# Revit family: P190780JX-228c_JFC2089BEP_StainlessSteel_JA_Refrigeraton_FS_FDBM
name_source: partatom
category: Specialty Equipment
units: mm (PartAtom-declared; Revit-internal decimal feet)

## family parameters
Always vertical = Yes
Cut with Voids When Loaded = No
Enable Cutting in Views = No
Maintain Annotation Orientation = No
Part Type = Normal
Room Calculation Point = No
Round Connector Dimension = Use Diameter
Shared = No
Work Plane-Based = No

## types (1)
- JFC2089BEP
    Accent Material = ARCAT - Metal - Steel - Black
    Amps = 20 A
    Body Material = ARCAT - Metal - Steel - Stainless
    Clearance Material = ARCAT - Clearance
    Default Elevation = 0"
    Depth = 29 7/8"
    Description = 69” Counter-Depth, French Door Refrigerator with Internal Water/Ice Dispensers
Réfrigérateur à profondeur de comptoir et portes françaises de 69 po avec distributeur d'eau/de glaçons intérieur
    Dimension Guide = http://access.whirlpool.com Guide&sku=JFC2089BEP&language=EN
http://access.whirlpool.com Guide&sku=JFC2089BEP&language=EN
    Door Material = ARCAT - Metal - Steel - Stainless
    Energy Guide = http://access.whirlpool.com Guide&sku=JFC2089BEP&language=EN
http://access.whirlpool.com Guide&sku=JFC2089BEP&language=FR
    Family Name = FS FDBM Pro
    Feature 1 = Counter Depth Design
Conception à profondeur de comptoir
    Feature 2 = TriSensor™ Electronic Climate Control
Régulateur électronique de la température TriSensor™
    Feature 3 = Glide-out Freezer Drawer with SmoothClose™ Drawer Track System
Tiroir de congélateur coulissant avec système de glissières de tiroir SmoothClose™
    Handle Material = ARCAT - Metal - Steel - Gray
    Height = 70 1/8"
    Manufacturer = Jenn Air
    Model = JFC2089BEP
    Voltage = 120 V
    Wheel Material = ARCAT - Plastic - Black
    Width = 35 5/8"

## geometry (parser evidence)
native form markers: Sweep x3
no freeform markers — native parametric forms only
